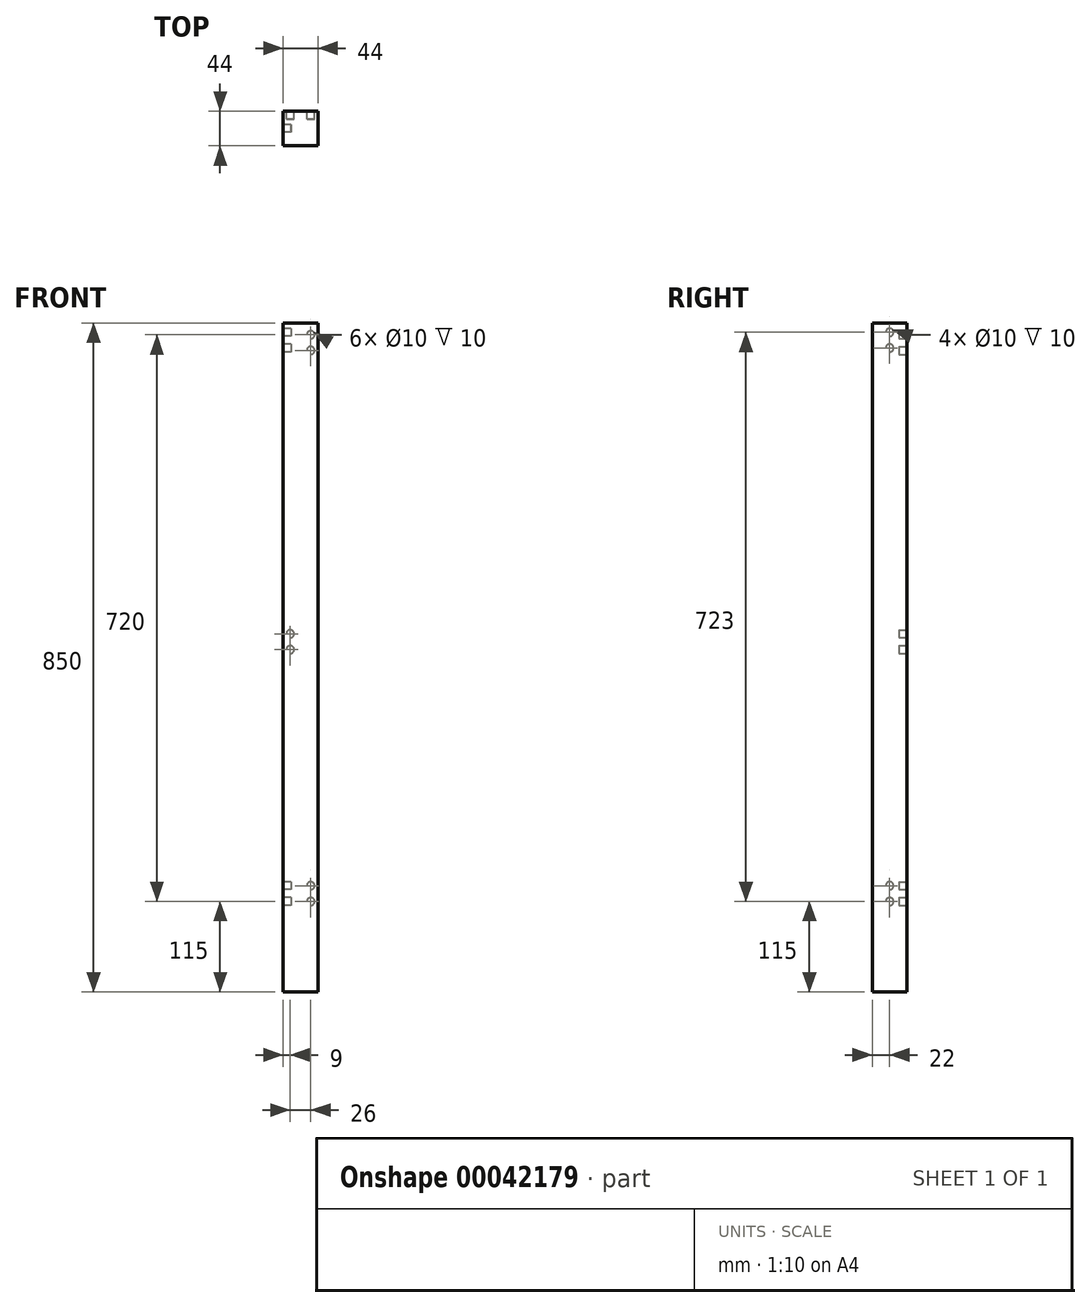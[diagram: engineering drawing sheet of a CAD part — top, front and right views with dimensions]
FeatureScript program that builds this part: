
annotation { "Feature Type Name" : "Feature", "Feature Type Description" : "" }
export const myFeature = defineFeature(function(context is Context, id is Id, definition is map)
    precondition{}
    {
        {
            var Q0;
            Q0=qCreatedBy(makeId("Top.planeOp"),FACE);
            var sketch = newSketch(context, id + "F0", { "sketchPlane" : qUnion([Q0])});
            skLineSegment(sketch, "E0", {"start": v(0, 0) * mm, "end": v(44, 0) * mm});
            skLineSegment(sketch, "E1", {"start": v(44, 0) * mm, "end": v(44, 44) * mm});
            skLineSegment(sketch, "E2", {"start": v(44, 44) * mm, "end": v(0, 44) * mm});
            skLineSegment(sketch, "E3", {"start": v(0, 44) * mm, "end": v(0, 0) * mm});
            skSolve(sketch);
        }
        {
            var Q0;
            Q0=makeQuery(id+"F0.imprint","IMPRINT",FACE,{"disambiguationData":[TD([[makeQuery(id+"F0.imprint","IMPRINT",EDGE,{"derivedFrom":sQuery(id+"F0.wireOp",EDGE,"E0")}),1.0]])]});
            extrude(context, id + "F1", {"entities" : qUnion([Q0]), "depth" : 850 * mm});
        }
        {
            var Q0;
            Q0=makeQuery(id+"F1.opExtrude","SWEPT_FACE",FACE,{"disambiguationData":[OSD([sQuery(id+"F0.wireOp",EDGE,"E2")])]});
            var sketch = newSketch(context, id + "F2", { "sketchPlane" : qUnion([Q0])});
            skCircle(sketch, "E4", {"center": v(-35, 135) * mm, "radius": 5 * mm});
            skLineSegment(sketch, "E5.direction1", {"start": v(-35, 135) * mm, "end": v(-9, 135) * mm, "construction": true});
            skLineSegment(sketch, "E6", {"start": v(-35, 135) * mm, "end": v(-35, 115) * mm, "construction": true});
            skCircle(sketch, "E7", {"center": v(-35, 115) * mm, "radius": 5 * mm});
            skLineSegment(sketch, "E8.direction1", {"start": v(-35, 115) * mm, "end": v(-9, 115) * mm, "construction": true});
            skCircle(sketch, "E9.0.1.0", {"center": v(-9, 435) * mm, "radius": 5 * mm});
            skLineSegment(sketch, "E9.direction1", {"start": v(-9, 135) * mm, "end": v(15, 135) * mm, "construction": true});
            skLineSegment(sketch, "E9.direction2", {"start": v(-9, 135) * mm, "end": v(-9, 435) * mm, "construction": true});
            skCircle(sketch, "E10.0.1.0", {"center": v(-35, 835) * mm, "radius": 5 * mm});
            skCircle(sketch, "E10.0.1.1", {"center": v(-35, 815) * mm, "radius": 5 * mm});
            skLineSegment(sketch, "E10.direction1", {"start": v(-35, 135) * mm, "end": v(-10, 135) * mm, "construction": true});
            skLineSegment(sketch, "E10.direction2", {"start": v(-35, 135) * mm, "end": v(-35, 835) * mm, "construction": true});
            skCircle(sketch, "E11.0.1.0", {"center": v(-9, 455) * mm, "radius": 5 * mm});
            skLineSegment(sketch, "E11.direction2", {"start": v(-9, 435) * mm, "end": v(-9, 455) * mm, "construction": true});
            skSolve(sketch);
        }
        {
            var Q0;
            Q0=makeQuery(id+"F2.imprint","IMPRINT",FACE,{"disambiguationData":[TD([[makeQuery(id+"F2.imprint","IMPRINT",EDGE,{"derivedFrom":sQuery(id+"F2.wireOp",EDGE,"8e0a97b6-d979-48df-9837-9e412e9741f4.1.0.0")}),1.0]])]});
            var Q1;
            Q1=makeQuery(id+"F2.imprint","IMPRINT",FACE,{"disambiguationData":[TD([[makeQuery(id+"F2.imprint","IMPRINT",EDGE,{"derivedFrom":sQuery(id+"F2.wireOp",EDGE,"f1c7cc12-a3ff-4c97-8521-861cfaabb000")}),1.0]])]});
            var Q2;
            Q2=makeQuery(id+"F2.imprint","IMPRINT",FACE,{"disambiguationData":[TD([[makeQuery(id+"F2.imprint","IMPRINT",EDGE,{"derivedFrom":sQuery(id+"F2.wireOp",EDGE,"8e0a97b6-d979-48df-9837-9e412e9741f4.0.1.0")}),1.0]])]});
            var Q3;
            Q3=makeQuery(id+"F2.imprint","IMPRINT",FACE,{"disambiguationData":[TD([[makeQuery(id+"F2.imprint","IMPRINT",EDGE,{"derivedFrom":sQuery(id+"F2.wireOp",EDGE,"8e0a97b6-d979-48df-9837-9e412e9741f4.1.1.0")}),1.0]])]});
            var Q4;
            Q4=makeQuery(id+"F2.imprint","IMPRINT",FACE,{"disambiguationData":[TD([[makeQuery(id+"F2.imprint","IMPRINT",EDGE,{"derivedFrom":sQuery(id+"F2.wireOp",EDGE,"E7")}),1.0]])]});
            var Q5;
            Q5=makeQuery(id+"F2.imprint","IMPRINT",FACE,{"disambiguationData":[TD([[makeQuery(id+"F2.imprint","IMPRINT",EDGE,{"derivedFrom":sQuery(id+"F2.wireOp",EDGE,"E8.1.0.0")}),1.0]])]});
            var Q6;
            Q6=makeQuery(id+"F2.imprint","IMPRINT",FACE,{"disambiguationData":[TD([[makeQuery(id+"F2.imprint","IMPRINT",EDGE,{"derivedFrom":sQuery(id+"F2.wireOp",EDGE,"E5.1.0.0")}),1.0]])]});
            var Q7;
            Q7=makeQuery(id+"F2.imprint","IMPRINT",FACE,{"disambiguationData":[TD([[makeQuery(id+"F2.imprint","IMPRINT",EDGE,{"derivedFrom":sQuery(id+"F2.wireOp",EDGE,"E4")}),1.0]])]});
            var Q8;
            Q8=makeQuery(id+"F2.imprint","IMPRINT",FACE,{"disambiguationData":[TD([[makeQuery(id+"F2.imprint","IMPRINT",EDGE,{"derivedFrom":sQuery(id+"F2.wireOp",EDGE,"E9.0.1.0")}),1.0]])]});
            var Q9;
            Q9=makeQuery(id+"F2.imprint","IMPRINT",FACE,{"disambiguationData":[TD([[makeQuery(id+"F2.imprint","IMPRINT",EDGE,{"derivedFrom":sQuery(id+"F2.wireOp",EDGE,"E9.0.1.1")}),1.0]])]});
            var Q10;
            Q10=makeQuery(id+"F2.imprint","IMPRINT",FACE,{"disambiguationData":[TD([[makeQuery(id+"F2.imprint","IMPRINT",EDGE,{"derivedFrom":sQuery(id+"F2.wireOp",EDGE,"E10.0.1.0")}),1.0]])]});
            var Q11;
            Q11=makeQuery(id+"F2.imprint","IMPRINT",FACE,{"disambiguationData":[TD([[makeQuery(id+"F2.imprint","IMPRINT",EDGE,{"derivedFrom":sQuery(id+"F2.wireOp",EDGE,"E10.0.1.1")}),1.0]])]});
            var Q12;
            Q12=makeQuery(id+"F2.imprint","IMPRINT",FACE,{"disambiguationData":[TD([[makeQuery(id+"F2.imprint","IMPRINT",EDGE,{"derivedFrom":sQuery(id+"F2.wireOp",EDGE,"E11.0.1.0")}),1.0]])]});
            extrude(context, id + "F3", {"entities" : qUnion([Q0, Q1, Q2, Q3, Q4, Q5, Q6, Q7, Q8, Q9, Q10, Q11, Q12]), "operationType" : NewBodyOperationType.REMOVE, "oppositeDirection" : true, "depth" : 10 * mm});
        }
        {
            var Q0;
            Q0=makeQuery(id+"F1.opExtrude","SWEPT_FACE",FACE,{"disambiguationData":[OSD([sQuery(id+"F0.wireOp",EDGE,"E3")])]});
            var sketch = newSketch(context, id + "F4", { "sketchPlane" : qUnion([Q0])});
            skCircle(sketch, "E12", {"center": v(-22, 135) * mm, "radius": 5 * mm});
            skCircle(sketch, "E13.0.1.0", {"center": v(-22, 115) * mm, "radius": 5 * mm});
            skLineSegment(sketch, "E13.direction1", {"start": v(-22, 135) * mm, "end": v(15, 135) * mm, "construction": true});
            skLineSegment(sketch, "E13.direction2", {"start": v(-22, 135) * mm, "end": v(-22, 115) * mm, "construction": true});
            skCircle(sketch, "E14.0.1.0", {"center": v(-22, 838) * mm, "radius": 5 * mm});
            skCircle(sketch, "E14.0.1.1", {"center": v(-22, 818) * mm, "radius": 5 * mm});
            skLineSegment(sketch, "E14.direction2", {"start": v(-22, 135) * mm, "end": v(-22, 838) * mm, "construction": true});
            skSolve(sketch);
        }
        {
            var Q0;
            Q0=makeQuery(id+"F4.imprint","IMPRINT",FACE,{"disambiguationData":[TD([[makeQuery(id+"F4.imprint","IMPRINT",EDGE,{"derivedFrom":sQuery(id+"F4.wireOp",EDGE,"E12")}),1.0]])]});
            var Q1;
            Q1=makeQuery(id+"F4.imprint","IMPRINT",FACE,{"disambiguationData":[TD([[makeQuery(id+"F4.imprint","IMPRINT",EDGE,{"derivedFrom":sQuery(id+"F4.wireOp",EDGE,"E13.0.1.0")}),1.0]])]});
            var Q2;
            Q2=makeQuery(id+"F4.imprint","IMPRINT",FACE,{"disambiguationData":[TD([[makeQuery(id+"F4.imprint","IMPRINT",EDGE,{"derivedFrom":sQuery(id+"F4.wireOp",EDGE,"E14.0.1.0")}),1.0]])]});
            var Q3;
            Q3=makeQuery(id+"F4.imprint","IMPRINT",FACE,{"disambiguationData":[TD([[makeQuery(id+"F4.imprint","IMPRINT",EDGE,{"derivedFrom":sQuery(id+"F4.wireOp",EDGE,"E14.0.1.1")}),1.0]])]});
            extrude(context, id + "F5", {"entities" : qUnion([Q0, Q1, Q2, Q3]), "operationType" : NewBodyOperationType.REMOVE, "oppositeDirection" : true, "depth" : 10 * mm});
        }
    });
